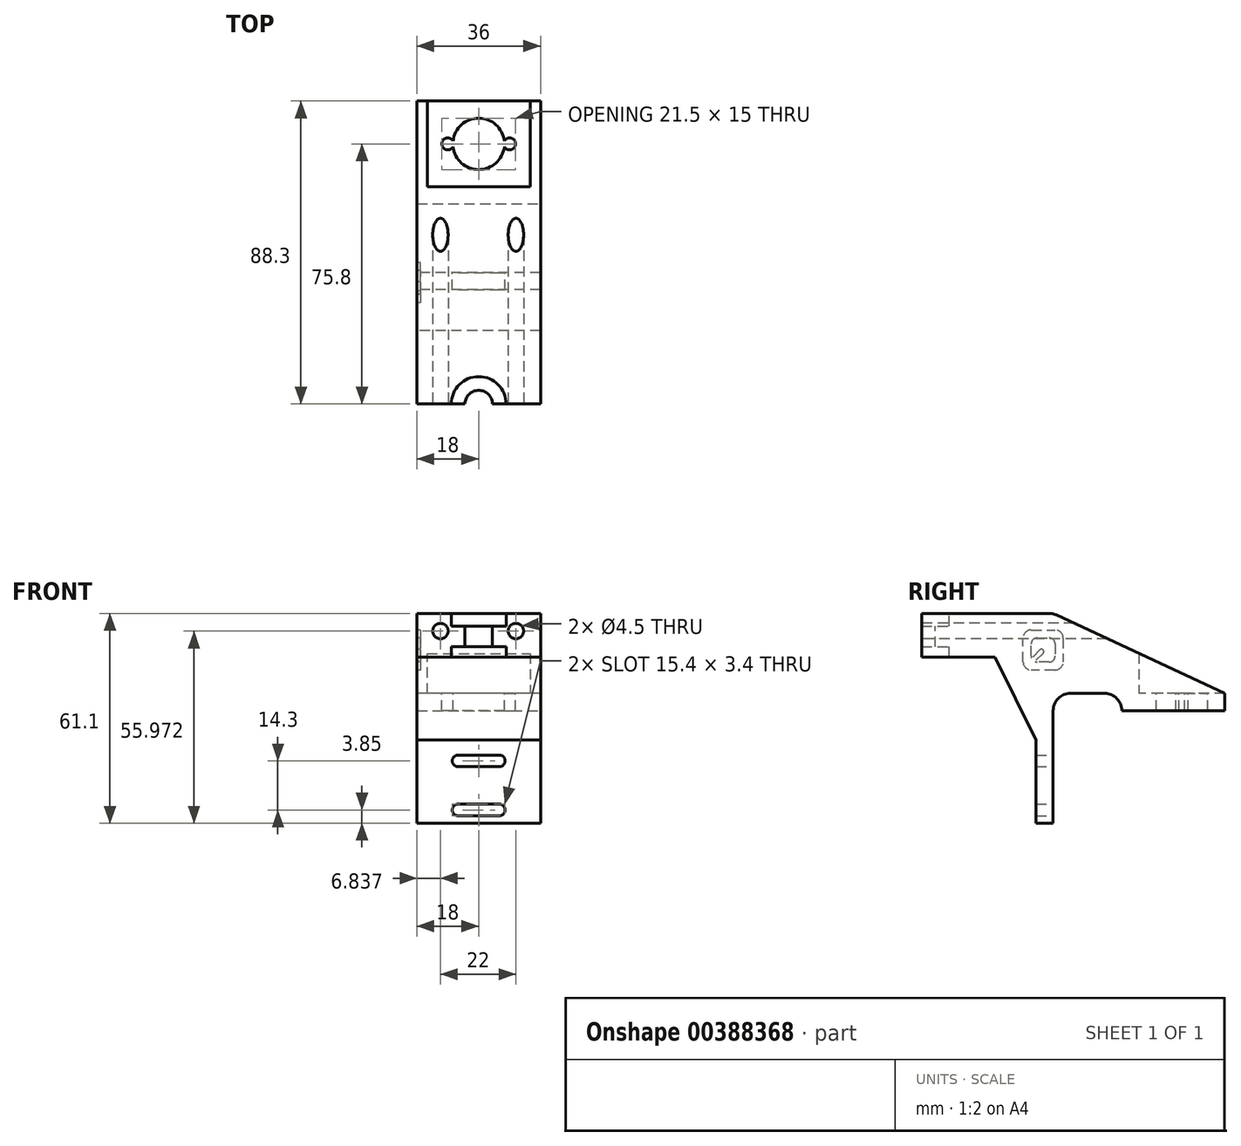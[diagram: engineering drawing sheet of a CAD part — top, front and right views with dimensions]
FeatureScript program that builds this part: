
annotation { "Feature Type Name" : "Feature", "Feature Type Description" : "" }
export const myFeature = defineFeature(function(context is Context, id is Id, definition is map)
    precondition{}
    {
        {
            var Q0;
            Q0=qCreatedBy(makeId("Front.planeOp"),FACE);
            var sketch = newSketch(context, id + "F0", { "sketchPlane" : qUnion([Q0])});
            skArc(sketch, "E0", {"start": v(-6, 16) * mm, "mid": v(-7.7, 14.3) * mm, "end": v(-6, 12.6) * mm});
            skArc(sketch, "E1", {"start": v(6, 12.6) * mm, "mid": v(7.7, 14.3) * mm, "end": v(6, 16) * mm});
            skArc(sketch, "E2", {"start": v(-6, 1.7) * mm, "mid": v(-7.7, 0) * mm, "end": v(-6, -1.7) * mm});
            skArc(sketch, "E3", {"start": v(6, -1.7) * mm, "mid": v(7.7, 0) * mm, "end": v(6, 1.7) * mm});
            skLineSegment(sketch, "E4", {"start": v(-6, 14.3) * mm, "end": v(6, 14.3) * mm, "construction": true});
            skLineSegment(sketch, "E5", {"start": v(6, 0) * mm, "end": v(6, 14.3) * mm, "construction": true});
            skLineSegment(sketch, "E6", {"start": v(-6, 0) * mm, "end": v(6, 0) * mm, "construction": true});
            skLineSegment(sketch, "E7", {"start": v(-6, 14.3) * mm, "end": v(-6, 0) * mm, "construction": true});
            skLineSegment(sketch, "E8.bottom", {"start": v(-15, 18.15) * mm, "end": v(15, 18.15) * mm});
            skLineSegment(sketch, "E8.top", {"start": v(-15, -3.85) * mm, "end": v(15, -3.85) * mm});
            skLineSegment(sketch, "E8.left", {"start": v(-15, 18.15) * mm, "end": v(-15, -3.85) * mm});
            skLineSegment(sketch, "E8.right", {"start": v(15, 18.15) * mm, "end": v(15, -3.85) * mm});
            skLineSegment(sketch, "E9", {"start": v(0, 14.3) * mm, "end": v(0, 18.15) * mm, "construction": true});
            skLineSegment(sketch, "E10", {"start": v(0, 0) * mm, "end": v(0, -3.85) * mm, "construction": true});
            skLineSegment(sketch, "E11", {"start": v(-6, 7.15) * mm, "end": v(-15, 7.15) * mm, "construction": true});
            skLineSegment(sketch, "E12", {"start": v(6, 7.15) * mm, "end": v(15, 7.15) * mm, "construction": true});
            skLineSegment(sketch, "E13", {"start": v(-6, 16) * mm, "end": v(6, 16) * mm});
            skLineSegment(sketch, "E14", {"start": v(-6, 12.6) * mm, "end": v(6, 12.6) * mm});
            skLineSegment(sketch, "E15", {"start": v(-6, 16) * mm, "end": v(-6, 12.6) * mm, "construction": true});
            skLineSegment(sketch, "E16", {"start": v(6, 16) * mm, "end": v(6, 12.6) * mm, "construction": true});
            skLineSegment(sketch, "E17", {"start": v(-6, 1.7) * mm, "end": v(6, 1.7) * mm});
            skLineSegment(sketch, "E18", {"start": v(-6, -1.7) * mm, "end": v(6, -1.7) * mm});
            skSolve(sketch);
        }
        {
            var Q0;
            Q0=makeQuery(id+"F0.imprint","IMPRINT",FACE,{"disambiguationData":[TD([[makeQuery(id+"F0.imprint","IMPRINT",EDGE,{"derivedFrom":sQuery(id+"F0.wireOp",EDGE,"E0")}),-1.0]])]});
            extrude(context, id + "F1", {"entities" : qUnion([Q0]), "depth" : 5 * mm});
        }
        {
            var Q0;
            Q0=makeQuery(id+"F1.opExtrude","SWEPT_FACE",FACE,{"disambiguationData":[OSD([sQuery(id+"F0.wireOp",EDGE,"E8.bottom")])]});
            extrude(context, id + "F2", {"entities" : qUnion([Q0]), "operationType" : NewBodyOperationType.ADD, "depth" : 39.1 * mm});
        }
        {
            var Q0;
            {var subQ0=sQuery(id+"F0.wireOp",EDGE,"E8.bottom");Q0=makeQuery(id+"F2.boolean.opBoolean","MERGE",FACE,{"derivedFrom":[makeQuery(id+"F1.opExtrude","CAP_FACE",FACE,{"disambiguationData":[OSD([sQuery(id+"F0.wireOp",EDGE,"E0"),sQuery(id+"F0.wireOp",EDGE,"E1"),sQuery(id+"F0.wireOp",EDGE,"E2"),sQuery(id+"F0.wireOp",EDGE,"E3"),subQ0,sQuery(id+"F0.wireOp",EDGE,"E8.top"),sQuery(id+"F0.wireOp",EDGE,"E8.left"),sQuery(id+"F0.wireOp",EDGE,"E8.right")])],"isStart":false}),makeQuery(id+"F2.opExtrude","SWEPT_FACE",FACE,{"disambiguationData":[OSD([subQ0]),TDD([makeQuery(id+"F1.opExtrude","CAP_EDGE",EDGE,{"disambiguationData":[OSD([subQ0])],"isStart":false})])]})]});}
            var sketch = newSketch(context, id + "F3", { "sketchPlane" : qUnion([Q0])});
            skLineSegment(sketch, "E19", {"start": v(-15, 44.55) * mm, "end": v(15, 44.55) * mm});
            skSolve(sketch);
        }
        {
            var Q0;
            {var subQ0=sQuery(id+"F3.wireOp",EDGE,"E19");Q0=makeQuery(id+"F3.imprint","IMPRINT",FACE,{"disambiguationData":[TD([[makeQuery(id+"F3.imprint","IMPRINT",EDGE,{"derivedFrom":subQ0}),1.0]])]});}
            extrude(context, id + "F4", {"entities" : qUnion([Q0]), "operationType" : NewBodyOperationType.ADD, "depth" : 50 * mm});
        }
        {
            var Q0;
            Q0=makeQuery(id+"F4.opExtrude","CAP_FACE",FACE,{"disambiguationData":[OSD([sQuery(id+"F0.wireOp",EDGE,"E8.bottom"),sQuery(id+"F0.wireOp",EDGE,"E8.left"),sQuery(id+"F0.wireOp",EDGE,"E8.right"),sQuery(id+"F3.wireOp",EDGE,"E19")])],"isStart":false});
            cPlane(context, id + "F5", {"entities" : qUnion([Q0]), "cplaneType" : CPlaneType.OFFSET, "offset" : 16.7 * mm, "oppositeDirection" : true, "width" : 150 * mm, "height" : 150 * mm});
        }
        {
            var Q0;
            Q0=qCreatedBy(id+"F5.planeOp",FACE);
            var sketch = newSketch(context, id + "F6", { "sketchPlane" : qUnion([Q0])});
            skLineSegment(sketch, "E20", {"start": v(0, 57.25) * mm, "end": v(8, 57.25) * mm});
            skLineSegment(sketch, "E21", {"start": v(8, 57.25) * mm, "end": v(8, 53.55) * mm});
            skLineSegment(sketch, "E22", {"start": v(8, 53.55) * mm, "end": v(4, 53.55) * mm});
            skLineSegment(sketch, "E23", {"start": v(4, 53.55) * mm, "end": v(4, 47.55) * mm});
            skLineSegment(sketch, "E24", {"start": v(4, 47.55) * mm, "end": v(8, 47.55) * mm});
            skLineSegment(sketch, "E25", {"start": v(8, 47.55) * mm, "end": v(8, 44.55) * mm});
            skLineSegment(sketch, "E26", {"start": v(8, 44.55) * mm, "end": v(0, 44.55) * mm});
            skLineSegment(sketch, "E27", {"start": v(0, 44.55) * mm, "end": v(0, 57.25) * mm});
            skSolve(sketch);
        }
        {
            var Q0;
            Q0 = qSketchRegion(id + "F6", true);
            var Q1;
            Q1=sQuery(id+"F6.wireOp",EDGE,"E27");
            revolve(context, id + "F7", {"operationType" : NewBodyOperationType.REMOVE, "entities" : qUnion([Q0]), "axis" : qUnion([Q1]), "revolveType" : RevolveType.FULL, "oppositeDirection" : true});
        }
        {
            var Q0;
            {var subQ0=sQuery(id+"F0.wireOp",EDGE,"E8.bottom");Q0=makeQuery(id+"F2.boolean.opBoolean","MERGE",FACE,{"derivedFrom":[makeQuery(id+"F1.opExtrude","CAP_FACE",FACE,{"disambiguationData":[OSD([sQuery(id+"F0.wireOp",EDGE,"E0"),sQuery(id+"F0.wireOp",EDGE,"E1"),sQuery(id+"F0.wireOp",EDGE,"E2"),sQuery(id+"F0.wireOp",EDGE,"E3"),subQ0,sQuery(id+"F0.wireOp",EDGE,"E8.top"),sQuery(id+"F0.wireOp",EDGE,"E8.left"),sQuery(id+"F0.wireOp",EDGE,"E8.right")])],"isStart":true}),makeQuery(id+"F2.opExtrude","SWEPT_FACE",FACE,{"disambiguationData":[OSD([subQ0]),TDD([makeQuery(id+"F1.opExtrude","CAP_EDGE",EDGE,{"disambiguationData":[OSD([subQ0])],"isStart":true})])]})]});}
            var sketch = newSketch(context, id + "F8", { "sketchPlane" : qUnion([Q0])});
            skLineSegment(sketch, "E28", {"start": v(-15, 33.95) * mm, "end": v(15, 33.95) * mm});
            skLineSegment(sketch, "E29", {"start": v(-15, 38.95) * mm, "end": v(15, 38.95) * mm});
            skSolve(sketch);
        }
        {
            var Q0;
            {var subQ0=sQuery(id+"F8.wireOp",EDGE,"E28");Q0=makeQuery(id+"F8.imprint","IMPRINT",FACE,{"disambiguationData":[TD([[makeQuery(id+"F8.imprint","IMPRINT",EDGE,{"derivedFrom":subQ0}),1.0]])]});}
            extrude(context, id + "F9", {"entities" : qUnion([Q0]), "operationType" : NewBodyOperationType.ADD, "depth" : 25 * mm});
        }
        {
            var Q0;
            Q0=makeQuery(id+"F9.opExtrude","SWEPT_FACE",FACE,{"disambiguationData":[OSD([sQuery(id+"F8.wireOp",EDGE,"E28")])]});
            var sketch = newSketch(context, id + "F10", { "sketchPlane" : qUnion([Q0])});
            skLineSegment(sketch, "E30", {"start": v(-15, -20) * mm, "end": v(15, -20) * mm});
            skSolve(sketch);
        }
        {
            var Q0;
            {var subQ0=sQuery(id+"F10.wireOp",EDGE,"E30");Q0=makeQuery(id+"F10.imprint","IMPRINT",FACE,{"disambiguationData":[TD([[makeQuery(id+"F10.imprint","IMPRINT",EDGE,{"derivedFrom":subQ0}),-1.0]])]});}
            extrude(context, id + "F11", {"entities" : qUnion([Q0]), "operationType" : NewBodyOperationType.ADD, "depth" : 5 * mm});
        }
        {
            var Q0;
            {var subQ0=sQuery(id+"F8.wireOp",EDGE,"E28");Q0=makeQuery(id+"F11.boolean.opBoolean","MERGE",FACE,{"derivedFrom":[makeQuery(id+"F9.opExtrude","CAP_FACE",FACE,{"disambiguationData":[OSD([sQuery(id+"F0.wireOp",EDGE,"E8.bottom"),sQuery(id+"F0.wireOp",EDGE,"E8.left"),sQuery(id+"F0.wireOp",EDGE,"E8.right"),subQ0,sQuery(id+"F8.wireOp",EDGE,"E29")])],"isStart":false}),makeQuery(id+"F11.opExtrude","SWEPT_FACE",FACE,{"disambiguationData":[OSD([subQ0])]})]});}
            var sketch = newSketch(context, id + "F12", { "sketchPlane" : qUnion([Q0])});
            skLineSegment(sketch, "E31", {"start": v(-15, 33.95) * mm, "end": v(15, 33.95) * mm});
            skSolve(sketch);
        }
        {
            var Q0;
            {var subQ0=sQuery(id+"F12.wireOp",EDGE,"E31");Q0=makeQuery(id+"F12.imprint","IMPRINT",FACE,{"disambiguationData":[TD([[makeQuery(id+"F12.imprint","IMPRINT",EDGE,{"derivedFrom":subQ0}),-1.0]])]});}
            extrude(context, id + "F13", {"entities" : qUnion([Q0]), "operationType" : NewBodyOperationType.ADD, "depth" : 25 * mm});
        }
        {
            var Q0;
            Q0=makeQuery(id+"F13.opExtrude","SWEPT_FACE",FACE,{"disambiguationData":[OSD([sQuery(id+"F12.wireOp",EDGE,"E31")])]});
            var sketch = newSketch(context, id + "F14", { "sketchPlane" : qUnion([Q0])});
            skArc(sketch, "E32", {"start": v(-7.45, 38.32) * mm, "mid": v(-10.75, 37.5) * mm, "end": v(-7.45, 36.68) * mm});
            skArc(sketch, "E33", {"start": v(7.45, 36.68) * mm, "mid": v(10.75, 37.5) * mm, "end": v(7.45, 38.32) * mm});
            skLineSegment(sketch, "E34", {"start": v(-9, 37.5) * mm, "end": v(9, 37.5) * mm, "construction": true});
            skLineSegment(sketch, "E35", {"start": v(-9, 37.5) * mm, "end": v(-15, 37.5) * mm, "construction": true});
            skLineSegment(sketch, "E36", {"start": v(9, 37.5) * mm, "end": v(15, 37.5) * mm, "construction": true});
            skLineSegment(sketch, "E37", {"start": v(0, 50) * mm, "end": v(0, 25) * mm, "construction": true});
            skArc(sketch, "E38", {"start": v(-7.45, 36.68) * mm, "mid": v(0, 30) * mm, "end": v(7.45, 36.68) * mm});
            skArc(sketch, "E39.trimOffspring", {"start": v(7.45, 38.32) * mm, "mid": v(0, 45) * mm, "end": v(-7.45, 38.32) * mm});
            skSolve(sketch);
        }
        {
            var Q0;
            Q0=makeQuery(id+"F14.imprint","IMPRINT",FACE,{"disambiguationData":[TD([[makeQuery(id+"F14.imprint","IMPRINT",EDGE,{"derivedFrom":sQuery(id+"F14.wireOp",EDGE,"E32")}),1.0]])]});
            extrude(context, id + "F15", {"entities" : qUnion([Q0]), "operationType" : NewBodyOperationType.REMOVE, "oppositeDirection" : true, "depth" : 25 * mm});
        }
        {
            var Q0;
            {var subQ0=sQuery(id+"F8.wireOp",EDGE,"E28");var subQ1=sQuery(id+"F0.wireOp",EDGE,"E8.right");var subQ2=sQuery(id+"F0.wireOp",EDGE,"E8.bottom");Q0=makeQuery(id+"F13.boolean.opBoolean","MERGE",FACE,{"derivedFrom":[makeQuery(id+"F11.boolean.opBoolean","MERGE",FACE,{"derivedFrom":[makeQuery(id+"F9.boolean.opBoolean","MERGE",FACE,{"derivedFrom":[makeQuery(id+"F4.boolean.opBoolean","MERGE",FACE,{"derivedFrom":[makeQuery(id+"F2.boolean.opBoolean","MERGE",FACE,{"derivedFrom":[makeQuery(id+"F1.opExtrude","SWEPT_FACE",FACE,{"disambiguationData":[OSD([subQ1])]}),makeQuery(id+"F2.opExtrude","SWEPT_FACE",FACE,{"disambiguationData":[OSD([subQ2,subQ1])]})]}),makeQuery(id+"F4.opExtrude","SWEPT_FACE",FACE,{"disambiguationData":[OSD([subQ2,subQ1])]})]}),makeQuery(id+"F9.opExtrude","SWEPT_FACE",FACE,{"disambiguationData":[OSD([subQ2,subQ1])]})]}),makeQuery(id+"F11.opExtrude","SWEPT_FACE",FACE,{"disambiguationData":[OSD([subQ2,subQ1,subQ0])]})]}),makeQuery(id+"F13.opExtrude","SWEPT_FACE",FACE,{"disambiguationData":[OSD([subQ2,subQ1,subQ0])]})]});}
            extrude(context, id + "F16", {"entities" : qUnion([Q0]), "operationType" : NewBodyOperationType.ADD, "depth" : 3 * mm});
        }
        {
            var Q0;
            Q0=makeQuery(id+"F16.opExtrude","CAP_FACE",FACE,{"disambiguationData":[OSD([sQuery(id+"F0.wireOp",EDGE,"E8.bottom"),sQuery(id+"F0.wireOp",EDGE,"E8.right"),sQuery(id+"F8.wireOp",EDGE,"E28")])],"isStart":false});
            var sketch = newSketch(context, id + "F17", { "sketchPlane" : qUnion([Q0])});
            skLineSegment(sketch, "E40", {"start": v(0, 57.25) * mm, "end": v(50, 33.95) * mm});
            skSolve(sketch);
        }
        {
            var Q0;
            Q0=makeQuery(id+"F17.imprint","IMPRINT",FACE,{"disambiguationData":[TD([[makeQuery(id+"F17.imprint","IMPRINT",EDGE,{"derivedFrom":sQuery(id+"F17.wireOp",EDGE,"E40")}),-1.0]])]});
            extrude(context, id + "F18", {"entities" : qUnion([Q0]), "operationType" : NewBodyOperationType.ADD, "oppositeDirection" : true, "depth" : 3 * mm});
        }
        {
            var Q0;
            {var subQ0=sQuery(id+"F8.wireOp",EDGE,"E28");var subQ1=sQuery(id+"F0.wireOp",EDGE,"E8.left");var subQ2=sQuery(id+"F0.wireOp",EDGE,"E8.bottom");Q0=makeQuery(id+"F13.boolean.opBoolean","MERGE",FACE,{"derivedFrom":[makeQuery(id+"F11.boolean.opBoolean","MERGE",FACE,{"derivedFrom":[makeQuery(id+"F9.boolean.opBoolean","MERGE",FACE,{"derivedFrom":[makeQuery(id+"F4.boolean.opBoolean","MERGE",FACE,{"derivedFrom":[makeQuery(id+"F2.boolean.opBoolean","MERGE",FACE,{"derivedFrom":[makeQuery(id+"F1.opExtrude","SWEPT_FACE",FACE,{"disambiguationData":[OSD([subQ1])]}),makeQuery(id+"F2.opExtrude","SWEPT_FACE",FACE,{"disambiguationData":[OSD([subQ2,subQ1])]})]}),makeQuery(id+"F4.opExtrude","SWEPT_FACE",FACE,{"disambiguationData":[OSD([subQ2,subQ1])]})]}),makeQuery(id+"F9.opExtrude","SWEPT_FACE",FACE,{"disambiguationData":[OSD([subQ2,subQ1])]})]}),makeQuery(id+"F11.opExtrude","SWEPT_FACE",FACE,{"disambiguationData":[OSD([subQ2,subQ1,subQ0])]})]}),makeQuery(id+"F13.opExtrude","SWEPT_FACE",FACE,{"disambiguationData":[OSD([subQ2,subQ1,subQ0])]})]});}
            extrude(context, id + "F19", {"entities" : qUnion([Q0]), "operationType" : NewBodyOperationType.ADD, "depth" : 3 * mm});
        }
        {
            var Q0;
            Q0=makeQuery(id+"F19.opExtrude","CAP_FACE",FACE,{"disambiguationData":[OSD([sQuery(id+"F0.wireOp",EDGE,"E8.bottom"),sQuery(id+"F0.wireOp",EDGE,"E8.left"),sQuery(id+"F8.wireOp",EDGE,"E28")])],"isStart":false});
            var sketch = newSketch(context, id + "F20", { "sketchPlane" : qUnion([Q0])});
            skLineSegment(sketch, "E41", {"start": v(-50, 33.95) * mm, "end": v(0, 57.25) * mm});
            skSolve(sketch);
        }
        {
            var Q0;
            Q0=makeQuery(id+"F20.imprint","IMPRINT",FACE,{"disambiguationData":[TD([[makeQuery(id+"F20.imprint","IMPRINT",EDGE,{"derivedFrom":sQuery(id+"F20.wireOp",EDGE,"E41")}),-1.0]])]});
            extrude(context, id + "F21", {"entities" : qUnion([Q0]), "operationType" : NewBodyOperationType.ADD, "oppositeDirection" : true, "depth" : 3 * mm});
        }
        {
            var Q0;
            Q0=makeQuery(id+"F18.opExtrude","CAP_FACE",FACE,{"disambiguationData":[OSD([sQuery(id+"F0.wireOp",EDGE,"E8.bottom"),sQuery(id+"F0.wireOp",EDGE,"E8.right"),sQuery(id+"F8.wireOp",EDGE,"E28"),sQuery(id+"F8.wireOp",EDGE,"E29"),sQuery(id+"F12.wireOp",EDGE,"E31"),sQuery(id+"F17.wireOp",EDGE,"E40")])],"isStart":false});
            var sketch = newSketch(context, id + "F22", { "sketchPlane" : qUnion([Q0])});
            skLineSegment(sketch, "E42", {"start": v(-25, 38.95) * mm, "end": v(-25, 45.6) * mm});
            skSolve(sketch);
        }
        {
            var Q0;
            {var subQ0=sQuery(id+"F22.wireOp",EDGE,"E42");Q0=makeQuery(id+"F22.imprint","IMPRINT",FACE,{"disambiguationData":[TD([[makeQuery(id+"F22.imprint","IMPRINT",EDGE,{"derivedFrom":subQ0}),-1.0]])]});}
            extrude(context, id + "F23", {"entities" : qUnion([Q0]), "operationType" : NewBodyOperationType.ADD, "endBound" : BoundingType.UP_TO_NEXT, "depth" : 25 * mm});
        }
        {
            var Q0;
            Q0=makeQuery(id+"F4.opExtrude","CAP_FACE",FACE,{"disambiguationData":[OSD([sQuery(id+"F0.wireOp",EDGE,"E8.bottom"),sQuery(id+"F0.wireOp",EDGE,"E8.left"),sQuery(id+"F0.wireOp",EDGE,"E8.right"),sQuery(id+"F3.wireOp",EDGE,"E19")])],"isStart":false});
            var sketch = newSketch(context, id + "F24", { "sketchPlane" : qUnion([Q0])});
            skCircle(sketch, "E43", {"center": v(-11.16, 52.12) * mm, "radius": 2.25 * mm});
            skCircle(sketch, "E44", {"center": v(10.84, 52.12) * mm, "radius": 2.25 * mm});
            skLineSegment(sketch, "E45", {"start": v(-11.16, 52.12) * mm, "end": v(10.84, 52.12) * mm, "construction": true});
            skLineSegment(sketch, "E46", {"start": v(0, 57.25) * mm, "end": v(-0.16, 44.55) * mm, "construction": true});
            skPoint(sketch, "E46.endSnap0", {"position": v(-0.16, 52.12) * mm});
            skSolve(sketch);
        }
        {
            var Q0;
            Q0=makeQuery(id+"F24.imprint","IMPRINT",FACE,{"disambiguationData":[TD([[makeQuery(id+"F24.imprint","IMPRINT",EDGE,{"derivedFrom":sQuery(id+"F24.wireOp",EDGE,"E43")}),1.0]])]});
            var Q1;
            Q1=makeQuery(id+"F24.imprint","IMPRINT",FACE,{"disambiguationData":[TD([[makeQuery(id+"F24.imprint","IMPRINT",EDGE,{"derivedFrom":sQuery(id+"F24.wireOp",EDGE,"E44")}),1.0]])]});
            extrude(context, id + "F25", {"entities" : qUnion([Q0, Q1]), "operationType" : NewBodyOperationType.REMOVE, "oppositeDirection" : true, "depth" : 500 * mm});
        }
        {
            var Q0;
            Q0=qCreatedBy(id+"F5.planeOp",FACE);
            var sketch = newSketch(context, id + "F26", { "sketchPlane" : qUnion([Q0])});
            skLineSegment(sketch, "E47.bottom", {"start": v(-33.75, 65.72) * mm, "end": v(34.34, 65.72) * mm});
            skLineSegment(sketch, "E47.top", {"start": v(-33.75, -7.1) * mm, "end": v(34.34, -7.1) * mm});
            skLineSegment(sketch, "E47.left", {"start": v(-33.75, 65.72) * mm, "end": v(-33.75, -7.1) * mm});
            skLineSegment(sketch, "E47.right", {"start": v(34.34, 65.72) * mm, "end": v(34.34, -7.1) * mm});
            skSolve(sketch);
        }
        {
            var Q0;
            Q0=makeQuery(id+"F26.imprint","IMPRINT",FACE,{"disambiguationData":[TD([[makeQuery(id+"F26.imprint","IMPRINT",EDGE,{"derivedFrom":sQuery(id+"F26.wireOp",EDGE,"E47.bottom")}),-1.0]])]});
            extrude(context, id + "F27", {"entities" : qUnion([Q0]), "operationType" : NewBodyOperationType.REMOVE, "depth" : 25 * mm});
        }
        {
            var Q0;
            {var subQ0=sQuery(id+"F8.wireOp",EDGE,"E28");var subQ1=sQuery(id+"F0.wireOp",EDGE,"E8.left");var subQ2=sQuery(id+"F0.wireOp",EDGE,"E8.bottom");Q0=makeQuery(id+"F21.boolean.opBoolean","MERGE",FACE,{"derivedFrom":[makeQuery(id+"F19.opExtrude","CAP_FACE",FACE,{"disambiguationData":[OSD([subQ2,subQ1,subQ0])],"isStart":false}),makeQuery(id+"F21.opExtrude","CAP_FACE",FACE,{"disambiguationData":[OSD([subQ2,subQ1,subQ0,sQuery(id+"F8.wireOp",EDGE,"E29"),sQuery(id+"F12.wireOp",EDGE,"E31"),sQuery(id+"F20.wireOp",EDGE,"E41")])],"isStart":true})]});}
            var sketch = newSketch(context, id + "F28", { "sketchPlane" : qUnion([Q0])});
            skLineSegment(sketch, "E48", {"start": v(5, 20.35) * mm, "end": v(16.93, 44.55) * mm});
            skSolve(sketch);
        }
        {
            var Q0;
            {var subQ0=sQuery(id+"F28.wireOp",EDGE,"E48");Q0=makeQuery(id+"F28.imprint","IMPRINT",FACE,{"disambiguationData":[TD([[makeQuery(id+"F28.imprint","IMPRINT",EDGE,{"derivedFrom":subQ0}),1.0]])]});}
            extrude(context, id + "F29", {"entities" : qUnion([Q0]), "operationType" : NewBodyOperationType.ADD, "oppositeDirection" : true, "depth" : 36 * mm});
        }
        {
            var Q0;
            Q0=makeQuery(id+"F29.opExtrude","SWEPT_EDGE",EDGE,{"disambiguationData":[OSD([sQuery(id+"F0.wireOp",EDGE,"E8.bottom"),sQuery(id+"F0.wireOp",EDGE,"E8.left"),sQuery(id+"F3.wireOp",EDGE,"E19"),sQuery(id+"F28.wireOp",EDGE,"E48")])]});
            var Q1;
            Q1=makeQuery(id+"F29.opExtrude","SWEPT_EDGE",EDGE,{"disambiguationData":[OSD([sQuery(id+"F0.wireOp",EDGE,"E8.bottom"),sQuery(id+"F0.wireOp",EDGE,"E8.left"),sQuery(id+"F28.wireOp",EDGE,"E48")])]});
            var Q2;
            {var subQ0=sQuery(id+"F17.wireOp",EDGE,"E40");var subQ1=sQuery(id+"F0.wireOp",EDGE,"E8.right");var subQ2=sQuery(id+"F0.wireOp",EDGE,"E8.bottom");var subQ3=sQuery(id+"F0.wireOp",EDGE,"E8.left");var subQ4=makeQuery(id+"F16.boolean.opBoolean","MERGE",EDGE,{"derivedFrom":[makeQuery(id+"F2.opExtrude","CAP_EDGE",EDGE,{"disambiguationData":[OSD([subQ2]),TDD([makeQuery(id+"F1.opExtrude","CAP_EDGE",EDGE,{"disambiguationData":[OSD([subQ2])],"isStart":true})])],"isStart":false}),makeQuery(id+"F16.opExtrude","SWEPT_EDGE",EDGE,{"disambiguationData":[OSD([subQ2,subQ1]),TDD([makeQuery(id+"F2.opExtrude","CAP_VERTEX",VERTEX,{"disambiguationData":[OSD([subQ2,subQ1]),TDD([makeQuery(id+"F1.opExtrude","CAP_VERTEX",VERTEX,{"disambiguationData":[OSD([subQ2,subQ1])],"isStart":true})])],"isStart":false})])]})]});var subQ5=makeQuery(id+"F19.boolean.opBoolean","MERGE",EDGE,{"derivedFrom":[makeQuery(id+"F18.boolean.opBoolean","SPLIT",EDGE,{"derivedFrom":subQ4}),makeQuery(id+"F19.opExtrude","SWEPT_EDGE",EDGE,{"disambiguationData":[OSD([subQ2,subQ3]),TDD([makeQuery(id+"F2.opExtrude","CAP_VERTEX",VERTEX,{"disambiguationData":[OSD([subQ2,subQ3]),TDD([makeQuery(id+"F1.opExtrude","CAP_VERTEX",VERTEX,{"disambiguationData":[OSD([subQ2,subQ3])],"isStart":true})])],"isStart":false})])]})]});Q2=makeQuery(id+"F23.boolean.opBoolean","MERGE",EDGE,{"derivedFrom":[makeQuery(id+"F18.boolean.opBoolean","MERGE",EDGE,{"derivedFrom":[subQ4,makeQuery(id+"F18.opExtrude","SWEPT_EDGE",EDGE,{"disambiguationData":[OSD([subQ2,subQ1,subQ0])]})]}),makeQuery(id+"F21.boolean.opBoolean","MERGE",EDGE,{"derivedFrom":[subQ5,makeQuery(id+"F21.opExtrude","SWEPT_EDGE",EDGE,{"disambiguationData":[OSD([subQ2,subQ3,sQuery(id+"F20.wireOp",EDGE,"E41")])]})]}),makeQuery(id+"F21.boolean.opBoolean","SPLIT",EDGE,{"derivedFrom":subQ5}),makeQuery(id+"F23.opExtrude","SWEPT_EDGE",EDGE,{"disambiguationData":[OSD([subQ2,subQ1,subQ0])]})]});}
            var Q3;
            {var subQ0=sQuery(id+"F10.wireOp",EDGE,"E30");var subQ1=sQuery(id+"F8.wireOp",EDGE,"E28");var subQ2=sQuery(id+"F0.wireOp",EDGE,"E8.left");var subQ3=sQuery(id+"F0.wireOp",EDGE,"E8.bottom");var subQ4=sQuery(id+"F0.wireOp",EDGE,"E8.right");Q3=makeQuery(id+"F19.boolean.opBoolean","MERGE",EDGE,{"derivedFrom":[makeQuery(id+"F16.boolean.opBoolean","MERGE",EDGE,{"derivedFrom":[makeQuery(id+"F11.opExtrude","CAP_EDGE",EDGE,{"disambiguationData":[OSD([subQ0])],"isStart":true}),makeQuery(id+"F16.opExtrude","SWEPT_EDGE",EDGE,{"disambiguationData":[OSD([subQ3,subQ4,subQ1,subQ0]),TDD([makeQuery(id+"F11.opExtrude","CAP_VERTEX",VERTEX,{"disambiguationData":[OSD([subQ3,subQ4,subQ1,subQ0])],"isStart":true})])]})]}),makeQuery(id+"F19.opExtrude","SWEPT_EDGE",EDGE,{"disambiguationData":[OSD([subQ3,subQ2,subQ1,subQ0]),TDD([makeQuery(id+"F11.opExtrude","CAP_VERTEX",VERTEX,{"disambiguationData":[OSD([subQ3,subQ2,subQ1,subQ0])],"isStart":true})])]})]});}
            var Q4;
            {var subQ0=sQuery(id+"F8.wireOp",EDGE,"E28");var subQ1=sQuery(id+"F0.wireOp",EDGE,"E8.left");var subQ2=sQuery(id+"F0.wireOp",EDGE,"E8.bottom");var subQ3=sQuery(id+"F0.wireOp",EDGE,"E8.right");Q4=makeQuery(id+"F19.boolean.opBoolean","MERGE",EDGE,{"derivedFrom":[makeQuery(id+"F16.boolean.opBoolean","MERGE",EDGE,{"derivedFrom":[makeQuery(id+"F9.opExtrude","CAP_EDGE",EDGE,{"disambiguationData":[OSD([subQ0])],"isStart":true}),makeQuery(id+"F16.opExtrude","SWEPT_EDGE",EDGE,{"disambiguationData":[OSD([subQ2,subQ3,subQ0]),TDD([makeQuery(id+"F9.opExtrude","CAP_VERTEX",VERTEX,{"disambiguationData":[OSD([subQ2,subQ3,subQ0])],"isStart":true})])]})]}),makeQuery(id+"F19.opExtrude","SWEPT_EDGE",EDGE,{"disambiguationData":[OSD([subQ2,subQ1,subQ0]),TDD([makeQuery(id+"F9.opExtrude","CAP_VERTEX",VERTEX,{"disambiguationData":[OSD([subQ2,subQ1,subQ0])],"isStart":true})])]})]});}
            fillet(context, id + "F30", {"entities" : qUnion([Q0, Q1, Q2, Q3, Q4]), "radius" : 5 * mm, "tangentPropagation" : true, "allowEdgeOverflow" : false});
        }
        {
            var Q0;
            {var subQ0=sQuery(id+"F0.wireOp",EDGE,"E8.left");var subQ1=sQuery(id+"F0.wireOp",EDGE,"E8.bottom");var subQ2=sQuery(id+"F8.wireOp",EDGE,"E28");Q0=makeQuery(id+"F29.boolean.opBoolean","MERGE",FACE,{"derivedFrom":[makeQuery(id+"F21.boolean.opBoolean","MERGE",FACE,{"derivedFrom":[makeQuery(id+"F19.opExtrude","CAP_FACE",FACE,{"disambiguationData":[OSD([subQ1,subQ0,subQ2])],"isStart":false}),makeQuery(id+"F21.opExtrude","CAP_FACE",FACE,{"disambiguationData":[OSD([subQ1,subQ0,subQ2,sQuery(id+"F8.wireOp",EDGE,"E29"),sQuery(id+"F12.wireOp",EDGE,"E31"),sQuery(id+"F20.wireOp",EDGE,"E41")])],"isStart":true})]}),makeQuery(id+"F29.opExtrude","CAP_FACE",FACE,{"disambiguationData":[OSD([subQ1,subQ0,sQuery(id+"F3.wireOp",EDGE,"E19"),sQuery(id+"F28.wireOp",EDGE,"E48")])],"isStart":true})]});}
            var sketch = newSketch(context, id + "F31", { "sketchPlane" : qUnion([Q0])});
            skLineSegment(sketch, "E49", {"start": v(-0.58, 40.77) * mm, "end": v(6.42, 40.77) * mm});
            skLineSegment(sketch, "E50", {"start": v(8.75, 43.1) * mm, "end": v(8.75, 50.1) * mm});
            skLineSegment(sketch, "E51", {"start": v(6.42, 52.44) * mm, "end": v(-0.58, 52.44) * mm});
            skLineSegment(sketch, "E52", {"start": v(-2.92, 50.1) * mm, "end": v(-2.92, 43.1) * mm});
            skArc(sketch, "E53", {"start": v(-0.58, 52.44) * mm, "mid": v(-2.23, 51.75) * mm, "end": v(-2.92, 50.1) * mm});
            skArc(sketch, "E54", {"start": v(8.75, 50.1) * mm, "mid": v(8.07, 51.75) * mm, "end": v(6.42, 52.44) * mm});
            skArc(sketch, "E55", {"start": v(-2.92, 43.1) * mm, "mid": v(-2.23, 41.45) * mm, "end": v(-0.58, 40.77) * mm});
            skArc(sketch, "E56", {"start": v(6.42, 40.77) * mm, "mid": v(8.07, 41.45) * mm, "end": v(8.75, 43.1) * mm});
            skLineSegment(sketch, "E57", {"start": v(1.17, 43.1) * mm, "end": v(4.67, 43.1) * mm});
            skLineSegment(sketch, "E58", {"start": v(6.42, 44.85) * mm, "end": v(6.42, 48.35) * mm});
            skLineSegment(sketch, "E59", {"start": v(4.67, 50.1) * mm, "end": v(1.17, 50.1) * mm});
            skLineSegment(sketch, "E60", {"start": v(-0.58, 48.35) * mm, "end": v(-0.58, 44.85) * mm});
            skArc(sketch, "E61", {"start": v(1.17, 50.1) * mm, "mid": v(-0.07, 49.6) * mm, "end": v(-0.58, 48.35) * mm});
            skArc(sketch, "E62", {"start": v(6.42, 48.35) * mm, "mid": v(5.9, 49.6) * mm, "end": v(4.67, 50.1) * mm});
            skArc(sketch, "E63", {"start": v(-0.58, 44.85) * mm, "mid": v(-0.07, 43.62) * mm, "end": v(1.17, 43.1) * mm});
            skLineSegment(sketch, "E64", {"start": v(2.92, 46.6) * mm, "end": v(3, 46.69) * mm});
            skLineSegment(sketch, "E65", {"start": v(3.82, 46.69) * mm, "end": v(6.3, 44.21) * mm});
            skLineSegment(sketch, "E66", {"start": v(2.83, 45.7) * mm, "end": v(5.3, 43.22) * mm});
            skArc(sketch, "E67", {"start": v(3.82, 46.69) * mm, "mid": v(3.41, 46.86) * mm, "end": v(3, 46.69) * mm});
            skArc(sketch, "E68", {"start": v(2.83, 46.52) * mm, "mid": v(2.66, 46.1) * mm, "end": v(2.83, 45.7) * mm});
            skArc(sketch, "E69", {"start": v(4.67, 43.1) * mm, "mid": v(5, 43.13) * mm, "end": v(5.3, 43.22) * mm});
            skArc(sketch, "E70", {"start": v(6.3, 44.21) * mm, "mid": v(6.39, 44.53) * mm, "end": v(6.42, 44.85) * mm});
            skLineSegment(sketch, "E71", {"start": v(2.83, 46.52) * mm, "end": v(2.92, 46.6) * mm});
            skSolve(sketch);
        }
        {
            var Q0;
            Q0 = qSketchRegion(id + "F31", true);
            extrude(context, id + "F32", {"entities" : qUnion([Q0]), "operationType" : NewBodyOperationType.REMOVE, "oppositeDirection" : true, "depth" : 1 * mm});
        }
    });
